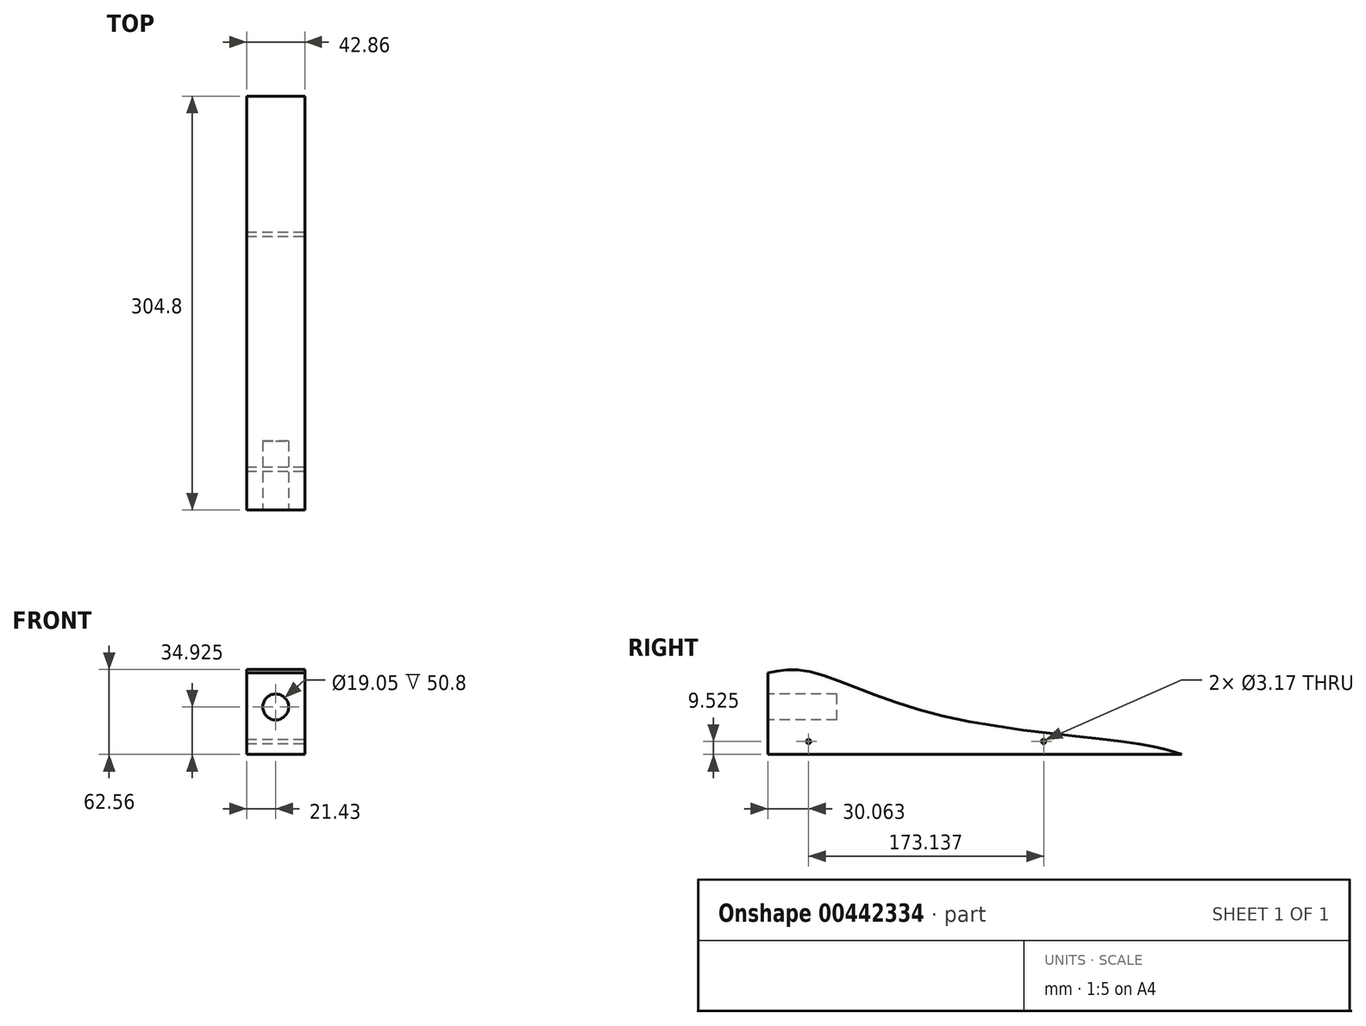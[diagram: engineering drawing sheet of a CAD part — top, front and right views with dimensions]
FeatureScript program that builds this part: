
annotation { "Feature Type Name" : "Feature", "Feature Type Description" : "" }
export const myFeature = defineFeature(function(context is Context, id is Id, definition is map)
    precondition{}
    {
        {
            var Q0;
            Q0=qCreatedBy(makeId("Right.planeOp"),FACE);
            var sketch = newSketch(context, id + "F0", { "sketchPlane" : qUnion([Q0])});
            skLineSegment(sketch, "E0", {"start": v(-152.4, 0) * mm, "end": v(152.4, 0) * mm});
            skLineSegment(sketch, "E1", {"start": v(-152.4, 0) * mm, "end": v(-152.4, 69.85) * mm});
            skLineSegment(sketch, "E2", {"start": v(152.4, 0) * mm, "end": v(152.4, 19.05) * mm});
            skLineSegment(sketch, "E3", {"start": v(152.4, 19.05) * mm, "end": v(-152.4, 69.85) * mm});
            skPoint(sketch, "E4.endSnap0", {"position": v(-152.4, 34.93) * mm});
            skLineSegment(sketch, "E5.0", {"start": v(-95.25, 50.8) * mm, "end": v(-152.4, 50.8) * mm, "construction": true});
            skLineSegment(sketch, "E5.1", {"start": v(-95.25, 50.8) * mm, "end": v(-95.25, 19.05) * mm, "construction": true});
            skLineSegment(sketch, "E5.2", {"start": v(-95.25, 19.05) * mm, "end": v(-152.4, 19.05) * mm, "construction": true});
            skSolve(sketch);
        }
        {
            var Q0;
            Q0=makeQuery(id+"F0.imprint","IMPRINT",FACE,{"disambiguationData":[TD([[makeQuery(id+"F0.imprint","IMPRINT",EDGE,{"derivedFrom":sQuery(id+"F0.wireOp",EDGE,"E0")}),1.0]])]});
            extrude(context, id + "F1", {"entities" : qUnion([Q0]), "depth" : 42.86 * mm, "symmetric" : true});
        }
        {
            var Q0;
            Q0=makeQuery(id+"F1.opExtrude","SWEPT_FACE",FACE,{"disambiguationData":[OSD([sQuery(id+"F0.wireOp",EDGE,"E1")])]});
            var sketch = newSketch(context, id + "F2", { "sketchPlane" : qUnion([Q0])});
            skLineSegment(sketch, "E6", {"start": v(21.43, 34.93) * mm, "end": v(0, 34.93) * mm, "construction": true});
            skCircle(sketch, "E7", {"center": v(0, 34.93) * mm, "radius": 9.53 * mm});
            skSolve(sketch);
        }
        {
            var Q0;
            Q0=makeQuery(id+"F2.imprint","IMPRINT",FACE,{"disambiguationData":[TD([[makeQuery(id+"F2.imprint","IMPRINT",EDGE,{"derivedFrom":sQuery(id+"F2.wireOp",EDGE,"E7")}),1.0]])]});
            var Q1;
            Q1=sQuery(id+"F2.wireOp",EDGE,"E7");
            extrude(context, id + "F3", {"entities" : qUnion([Q0]), "operationType" : NewBodyOperationType.REMOVE, "surfaceEntities" : qUnion([Q1]), "oppositeDirection" : true, "depth" : 50.8 * mm});
        }
        {
            var Q0;
            Q0=makeQuery(id+"F1.opExtrude","CAP_FACE",FACE,{"disambiguationData":[OSD([sQuery(id+"F0.wireOp",EDGE,"E0"),sQuery(id+"F0.wireOp",EDGE,"E1"),sQuery(id+"F0.wireOp",EDGE,"E2"),sQuery(id+"F0.wireOp",EDGE,"E3")])],"isStart":false});
            var sketch = newSketch(context, id + "F4", { "sketchPlane" : qUnion([Q0])});
            skLineSegment(sketch, "E8", {"start": v(-152.4, 34.93) * mm, "end": v(-152.4, 44.45) * mm, "construction": true});
            skLineSegment(sketch, "E9.0", {"start": v(-95.25, 19.05) * mm, "end": v(-152.4, 19.05) * mm, "construction": true});
            skLineSegment(sketch, "E9.1", {"start": v(-95.25, 50.8) * mm, "end": v(-95.25, 19.05) * mm, "construction": true});
            skLineSegment(sketch, "E9.2", {"start": v(-152.4, 50.8) * mm, "end": v(-95.25, 50.8) * mm, "construction": true});
            skLineSegment(sketch, "E10", {"start": v(57.15, 0) * mm, "end": v(57.15, 34.93) * mm, "construction": true});
            skLineSegment(sketch, "E11", {"start": v(-152.4, 44.45) * mm, "end": v(-101.6, 44.45) * mm, "construction": true});
            skLineSegment(sketch, "E12", {"start": v(-101.6, 44.45) * mm, "end": v(-101.6, 25.4) * mm, "construction": true});
            skLineSegment(sketch, "E13", {"start": v(-101.6, 25.4) * mm, "end": v(-152.4, 25.4) * mm, "construction": true});
            skFitSpline(sketch, "E14", {"points": [v(-152.4, 60.1) * mm, v(-124.46, 61.7) * mm, v(-32.9, 30.65) * mm, v(123.66, 7.3) * mm, v(152.4, 0) * mm], "startDerivative": vector(158.33, 33.47) * mm, "endDerivative": vector(131.76, -45.63) * mm});
            skCircle(sketch, "E15", {"center": v(-122.34, 9.53) * mm, "radius": 1.59 * mm});
            skCircle(sketch, "E16", {"center": v(50.8, 9.53) * mm, "radius": 1.59 * mm});
            skSolve(sketch);
        }
        {
            var Q0;
            {var subQ0=sQuery(id+"F4.wireOp",EDGE,"E14");Q0=makeQuery(id+"F4.imprint","IMPRINT",FACE,{"disambiguationData":[TD([[makeQuery(id+"F4.imprint","IMPRINT",EDGE,{"derivedFrom":subQ0}),-1.0]])]});}
            extrude(context, id + "F5", {"entities" : qUnion([Q0]), "operationType" : NewBodyOperationType.INTERSECT, "endBound" : BoundingType.THROUGH_ALL, "oppositeDirection" : true, "depth" : 25.4 * mm});
        }
    });
